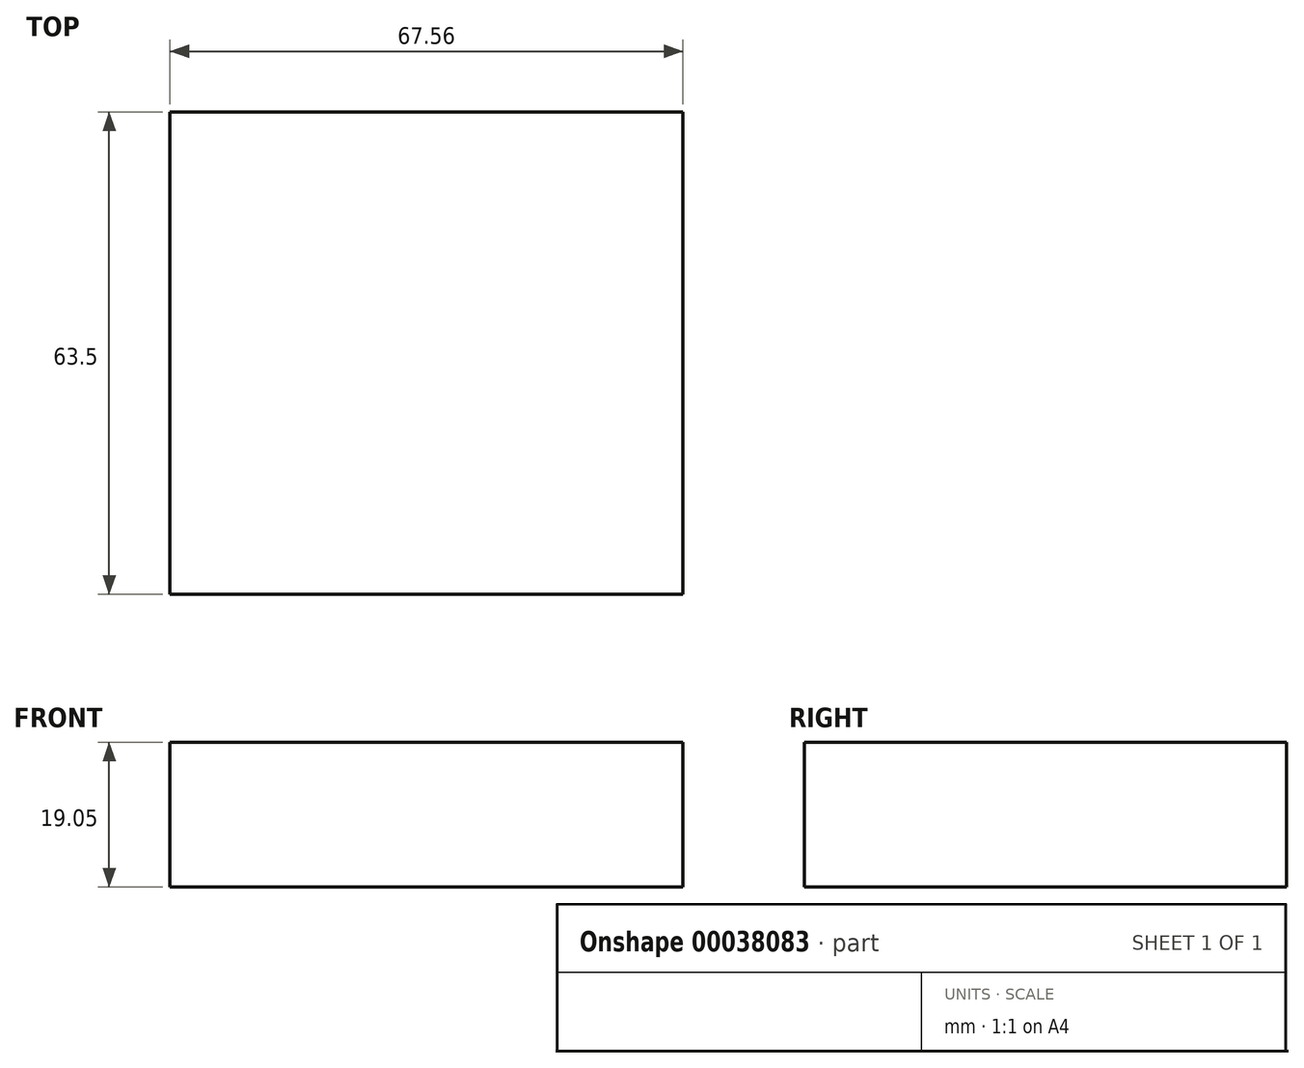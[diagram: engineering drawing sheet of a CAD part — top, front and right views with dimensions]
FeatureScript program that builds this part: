
annotation { "Feature Type Name" : "Feature", "Feature Type Description" : "" }
export const myFeature = defineFeature(function(context is Context, id is Id, definition is map)
    precondition{}
    {
        {
            var Q0;
            Q0=qCreatedBy(makeId("Top.planeOp"),FACE);
            var sketch = newSketch(context, id + "F0", { "sketchPlane" : qUnion([Q0])});
            skLineSegment(sketch, "E0.bottom", {"start": v(0, 0) * mm, "end": v(-67.56, 0) * mm});
            skLineSegment(sketch, "E0.top", {"start": v(0, -63.5) * mm, "end": v(-67.56, -63.5) * mm});
            skLineSegment(sketch, "E0.left", {"start": v(0, 0) * mm, "end": v(0, -63.5) * mm});
            skLineSegment(sketch, "E0.right", {"start": v(-67.56, 0) * mm, "end": v(-67.56, -63.5) * mm});
            skSolve(sketch);
        }
        {
            var Q0;
            Q0 = qSketchRegion(id + "F0", true);
            extrude(context, id + "F1", {"entities" : qUnion([Q0]), "depth" : 19.05 * mm});
        }
    });
